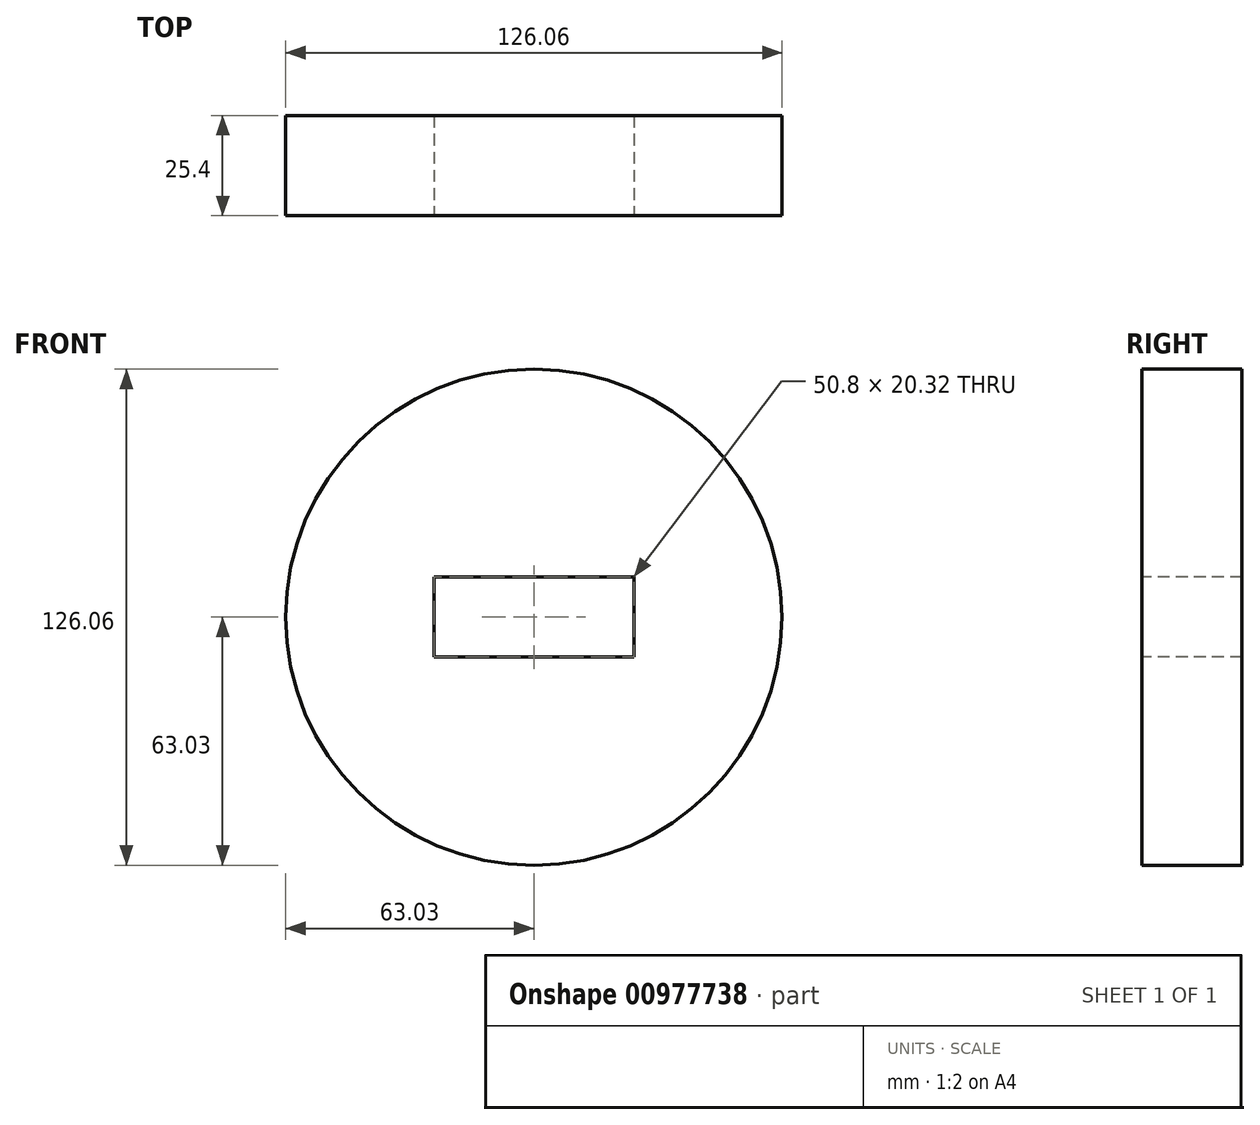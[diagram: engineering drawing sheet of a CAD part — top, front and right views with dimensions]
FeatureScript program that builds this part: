
annotation { "Feature Type Name" : "Feature", "Feature Type Description" : "" }
export const myFeature = defineFeature(function(context is Context, id is Id, definition is map)
    precondition{}
    {
        {
            var Q0;
            Q0=qCreatedBy(makeId("Front.planeOp"),FACE);
            var sketch = newSketch(context, id + "F0", { "sketchPlane" : qUnion([Q0])});
            skCircle(sketch, "E0", {"center": v(0, 0) * mm, "radius": 63.03 * mm});
            skSolve(sketch);
        }
        {
            var Q0;
            Q0=makeQuery(id+"F0.imprint","IMPRINT",FACE,{"disambiguationData":[TD([[makeQuery(id+"F0.imprint","IMPRINT",EDGE,{"derivedFrom":sQuery(id+"F0.wireOp",EDGE,"E0")}),1.0]])]});
            extrude(context, id + "F1", {"entities" : qUnion([Q0]), "endBound" : BoundingType.SYMMETRIC, "oppositeDirection" : true, "depth" : 25.4 * mm, "offsetDistance" : 25.4 * mm});
        }
        {
            var Q0;
            Q0=makeQuery(id+"F1.opExtrude","CAP_FACE",FACE,{"disambiguationData":[OSD([sQuery(id+"F0.wireOp",EDGE,"E0")])],"isStart":true});
            var sketch = newSketch(context, id + "F2", { "sketchPlane" : qUnion([Q0])});
            skLineSegment(sketch, "E1.bottom", {"start": v(25.4, -10.16) * mm, "end": v(-25.4, -10.16) * mm});
            skLineSegment(sketch, "E1.top", {"start": v(25.4, 10.16) * mm, "end": v(-25.4, 10.16) * mm});
            skLineSegment(sketch, "E1.left", {"start": v(25.4, -10.16) * mm, "end": v(25.4, 10.16) * mm});
            skLineSegment(sketch, "E1.right", {"start": v(-25.4, -10.16) * mm, "end": v(-25.4, 10.16) * mm});
            skPoint(sketch, "E1.middle", {"position": v(0, 0) * mm});
            skSolve(sketch);
        }
        {
            var Q0;
            Q0 = qSketchRegion(id + "F2", true);
            extrude(context, id + "F3", {"entities" : qUnion([Q0]), "operationType" : NewBodyOperationType.REMOVE, "endBound" : BoundingType.THROUGH_ALL, "oppositeDirection" : true, "depth" : 25.4 * mm, "offsetDistance" : 25.4 * mm});
        }
    });
